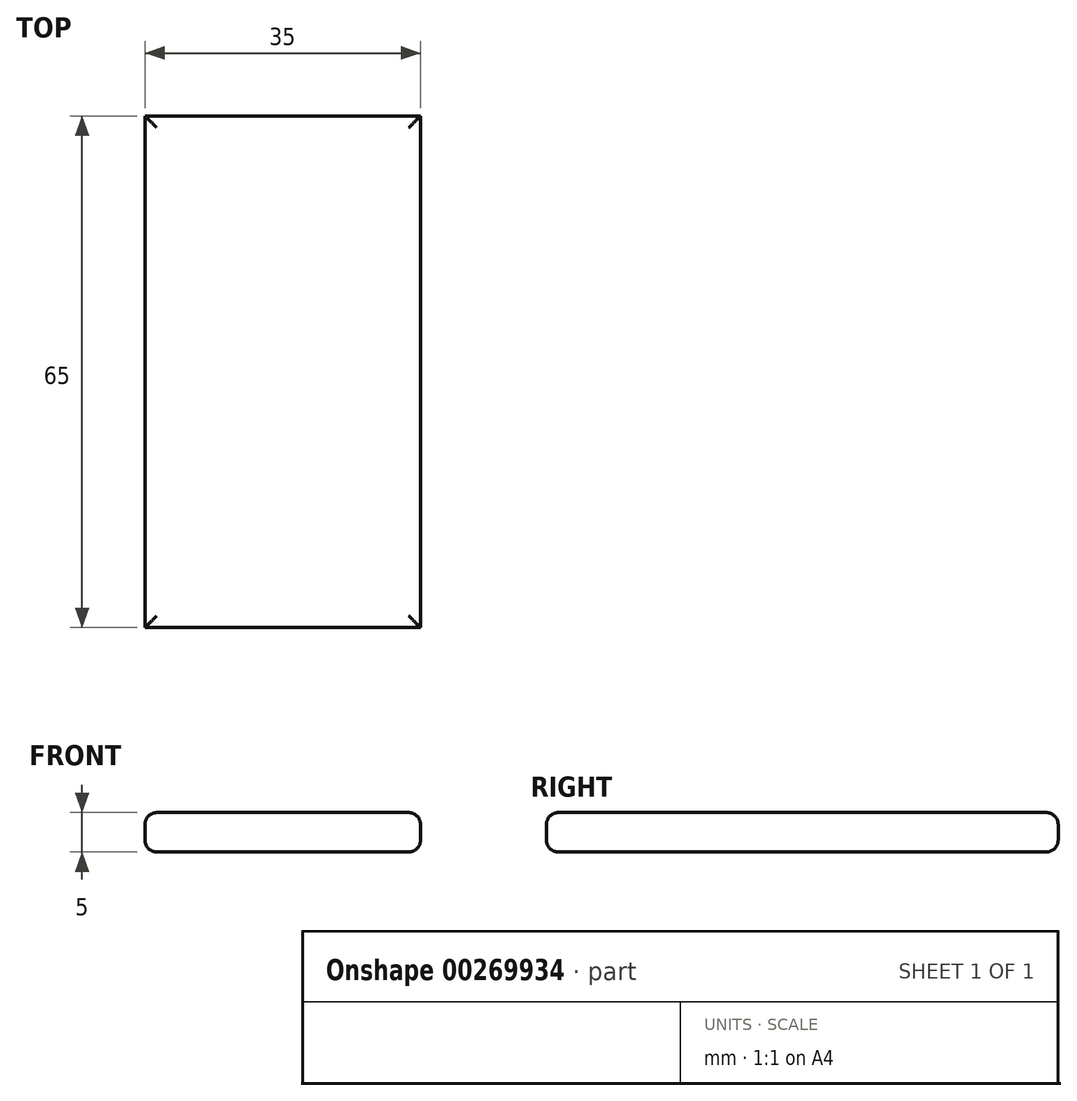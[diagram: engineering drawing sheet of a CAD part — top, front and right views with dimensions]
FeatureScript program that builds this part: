
annotation { "Feature Type Name" : "Feature", "Feature Type Description" : "" }
export const myFeature = defineFeature(function(context is Context, id is Id, definition is map)
    precondition{}
    {
        {
            var Q0;
            Q0=qCreatedBy(makeId("Top.planeOp"),FACE);
            var sketch = newSketch(context, id + "F0", { "sketchPlane" : qUnion([Q0])});
            skLineSegment(sketch, "E0.bottom", {"start": v(17.5, 32.7) * mm, "end": v(17.5, -32.3) * mm});
            skLineSegment(sketch, "E0.top", {"start": v(-17.5, 32.7) * mm, "end": v(-17.5, -32.3) * mm});
            skLineSegment(sketch, "E0.left", {"start": v(17.5, 32.7) * mm, "end": v(-17.5, 32.7) * mm});
            skLineSegment(sketch, "E0.right", {"start": v(17.5, -32.3) * mm, "end": v(-17.5, -32.3) * mm});
            skPoint(sketch, "E0.middle", {"position": v(0, 0.2) * mm});
            skSolve(sketch);
        }
        {
            var Q0;
            Q0=makeQuery(id+"F0.imprint","IMPRINT",FACE,{"disambiguationData":[TD([[makeQuery(id+"F0.imprint","IMPRINT",EDGE,{"derivedFrom":sQuery(id+"F0.wireOp",EDGE,"E0.bottom")}),-1.0]])]});
            extrude(context, id + "F1", {"entities" : qUnion([Q0]), "depth" : 5 * mm});
        }
        {
            var Q0;
            Q0=makeQuery(id+"F1.opExtrude","CAP_EDGE",EDGE,{"disambiguationData":[OSD([sQuery(id+"F0.wireOp",EDGE,"E0.top")])],"isStart":false});
            var Q1;
            Q1=makeQuery(id+"F1.opExtrude","CAP_EDGE",EDGE,{"disambiguationData":[OSD([sQuery(id+"F0.wireOp",EDGE,"E0.right")])],"isStart":false});
            var Q2;
            Q2=makeQuery(id+"F1.opExtrude","CAP_EDGE",EDGE,{"disambiguationData":[OSD([sQuery(id+"F0.wireOp",EDGE,"E0.bottom")])],"isStart":false});
            var Q3;
            Q3=makeQuery(id+"F1.opExtrude","CAP_EDGE",EDGE,{"disambiguationData":[OSD([sQuery(id+"F0.wireOp",EDGE,"E0.left")])],"isStart":false});
            var Q4;
            Q4=makeQuery(id+"F1.opExtrude","CAP_FACE",FACE,{"disambiguationData":[OSD([sQuery(id+"F0.wireOp",EDGE,"E0.bottom"),sQuery(id+"F0.wireOp",EDGE,"E0.top"),sQuery(id+"F0.wireOp",EDGE,"E0.left"),sQuery(id+"F0.wireOp",EDGE,"E0.right")])],"isStart":true});
            fillet(context, id + "F2", {"entities" : qUnion([Q0, Q1, Q2, Q3, Q4]), "radius" : 1.5 * mm, "tangentPropagation" : true, "allowEdgeOverflow" : false});
        }
    });
